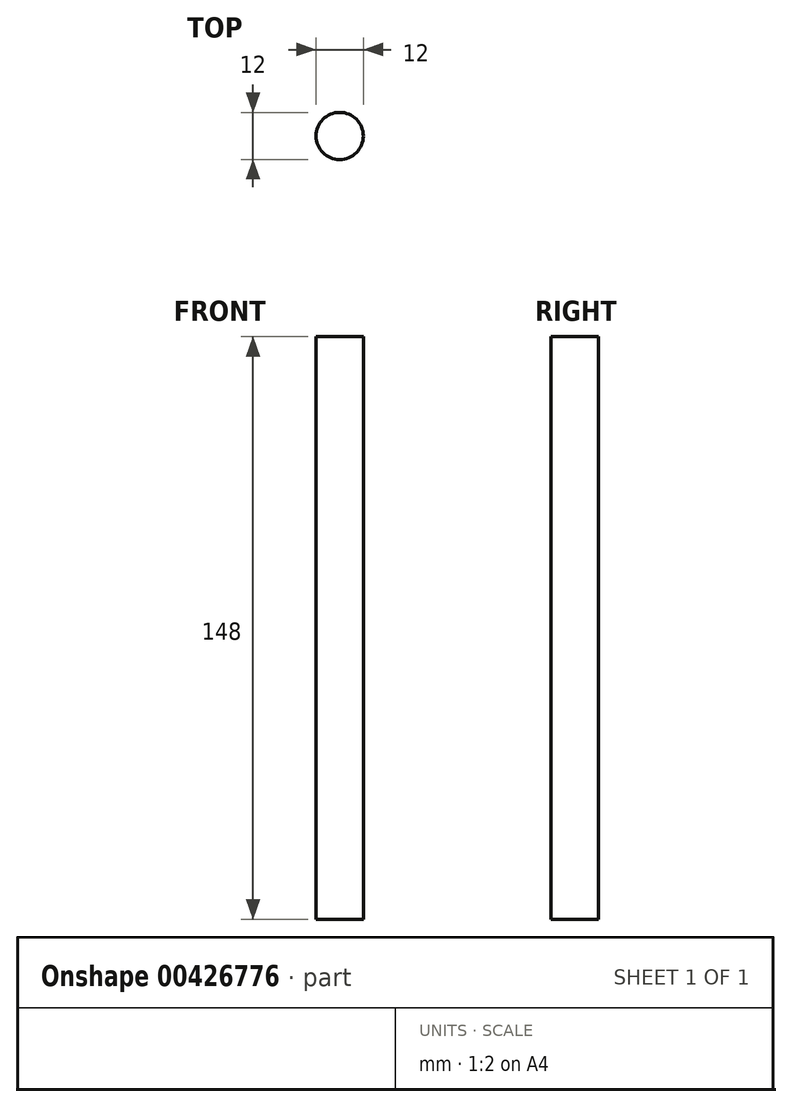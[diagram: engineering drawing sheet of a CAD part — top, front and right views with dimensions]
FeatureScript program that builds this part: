
annotation { "Feature Type Name" : "Feature", "Feature Type Description" : "" }
export const myFeature = defineFeature(function(context is Context, id is Id, definition is map)
    precondition{}
    {
        {
            var Q0;
            Q0=qCreatedBy(makeId("Top.planeOp"),FACE);
            var sketch = newSketch(context, id + "F0", { "sketchPlane" : qUnion([Q0])});
            skCircle(sketch, "E0", {"center": v(0, 0) * mm, "radius": 6 * mm});
            skSolve(sketch);
        }
        {
            var Q0;
            Q0=makeQuery(id+"F0.imprint","IMPRINT",FACE,{"disambiguationData":[TD([[makeQuery(id+"F0.imprint","IMPRINT",EDGE,{"derivedFrom":sQuery(id+"F0.wireOp",EDGE,"E0")}),1.0]])]});
            extrude(context, id + "F1", {"entities" : qUnion([Q0]), "depth" : 148 * mm});
        }
    });
